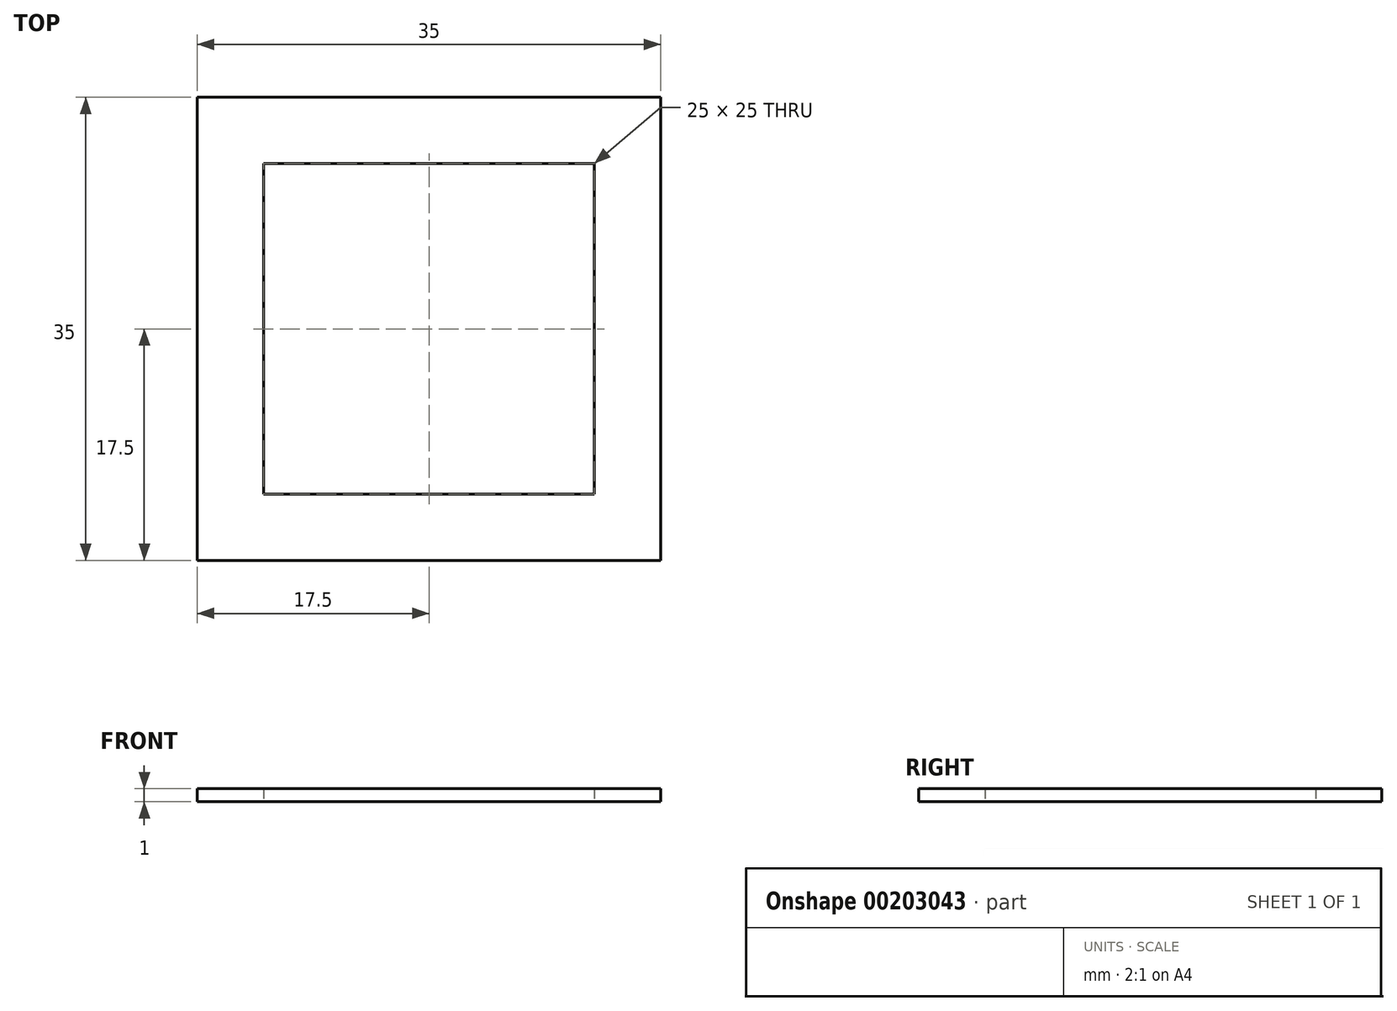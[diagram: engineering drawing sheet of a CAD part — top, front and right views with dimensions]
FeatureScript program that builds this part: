
annotation { "Feature Type Name" : "Feature", "Feature Type Description" : "" }
export const myFeature = defineFeature(function(context is Context, id is Id, definition is map)
    precondition{}
    {
        {
            var Q0;
            Q0=qCreatedBy(makeId("Top.planeOp"),FACE);
            var sketch = newSketch(context, id + "F0", { "sketchPlane" : qUnion([Q0])});
            skLineSegment(sketch, "E0.bottom", {"start": v(-12.5, 12.5) * mm, "end": v(12.5, 12.5) * mm});
            skLineSegment(sketch, "E0.top", {"start": v(-12.5, -12.5) * mm, "end": v(12.5, -12.5) * mm});
            skLineSegment(sketch, "E0.left", {"start": v(-12.5, 12.5) * mm, "end": v(-12.5, -12.5) * mm});
            skLineSegment(sketch, "E0.right", {"start": v(12.5, 12.5) * mm, "end": v(12.5, -12.5) * mm});
            skPoint(sketch, "E0.middle", {"position": v(0, 0) * mm});
            skLineSegment(sketch, "E1.bottom", {"start": v(17.5, 17.5) * mm, "end": v(-17.5, 17.5) * mm});
            skLineSegment(sketch, "E1.top", {"start": v(17.5, -17.5) * mm, "end": v(-17.5, -17.5) * mm});
            skLineSegment(sketch, "E1.left", {"start": v(17.5, 17.5) * mm, "end": v(17.5, -17.5) * mm});
            skLineSegment(sketch, "E1.right", {"start": v(-17.5, 17.5) * mm, "end": v(-17.5, -17.5) * mm});
            skSolve(sketch);
        }
        {
            var Q0;
            Q0=makeQuery(id+"F0.imprint","IMPRINT",FACE,{"disambiguationData":[TD([[makeQuery(id+"F0.imprint","IMPRINT",EDGE,{"derivedFrom":sQuery(id+"F0.wireOp",EDGE,"E0.bottom")}),1.0]])]});
            extrude(context, id + "F1", {"entities" : qUnion([Q0]), "depth" : 1 * mm});
        }
    });
